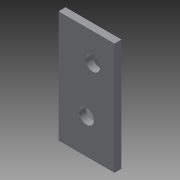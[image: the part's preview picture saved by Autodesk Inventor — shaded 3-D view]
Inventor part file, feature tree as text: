
AUTODESK INVENTOR PART (.ipt)
format: ipt  version: 2013 (Build 170138000, 138)  size: 91,136 bytes
history: native  units: in
note: dims shown in document units (in); Inventor stores cm internally (conversion verified against a paired STEP export)
features: extrude x3, sketch x3, reference x2
ambient origin geometry x8: Origin, YZ Plane, XZ Plane, XY Plane, X Axis, Y Axis, Z Axis, Center Point
bodies: Solid1 (feature_tree)
feature tree (8):
  extrude  "Extrusion1"  Depth=2.0in
  extrude  "Extrusion2"  Depth=1.0in TaperAngle=0.0deg
  extrude  "Extrusion3"  Depth=1.0in TaperAngle=0.0deg
  sketch  "Sketch1"  dims[d0=1.0in d1=2.0in]
  sketch  "Sketch2"  dims[d2=0.125in d3=0.0in d4=1.0in d5=0.0in]
  reference  "Reference1"
  reference  "Reference2"
  sketch  "Sketch3"  dims[d6=0.25in d7=1.0in d8=0.0in]
